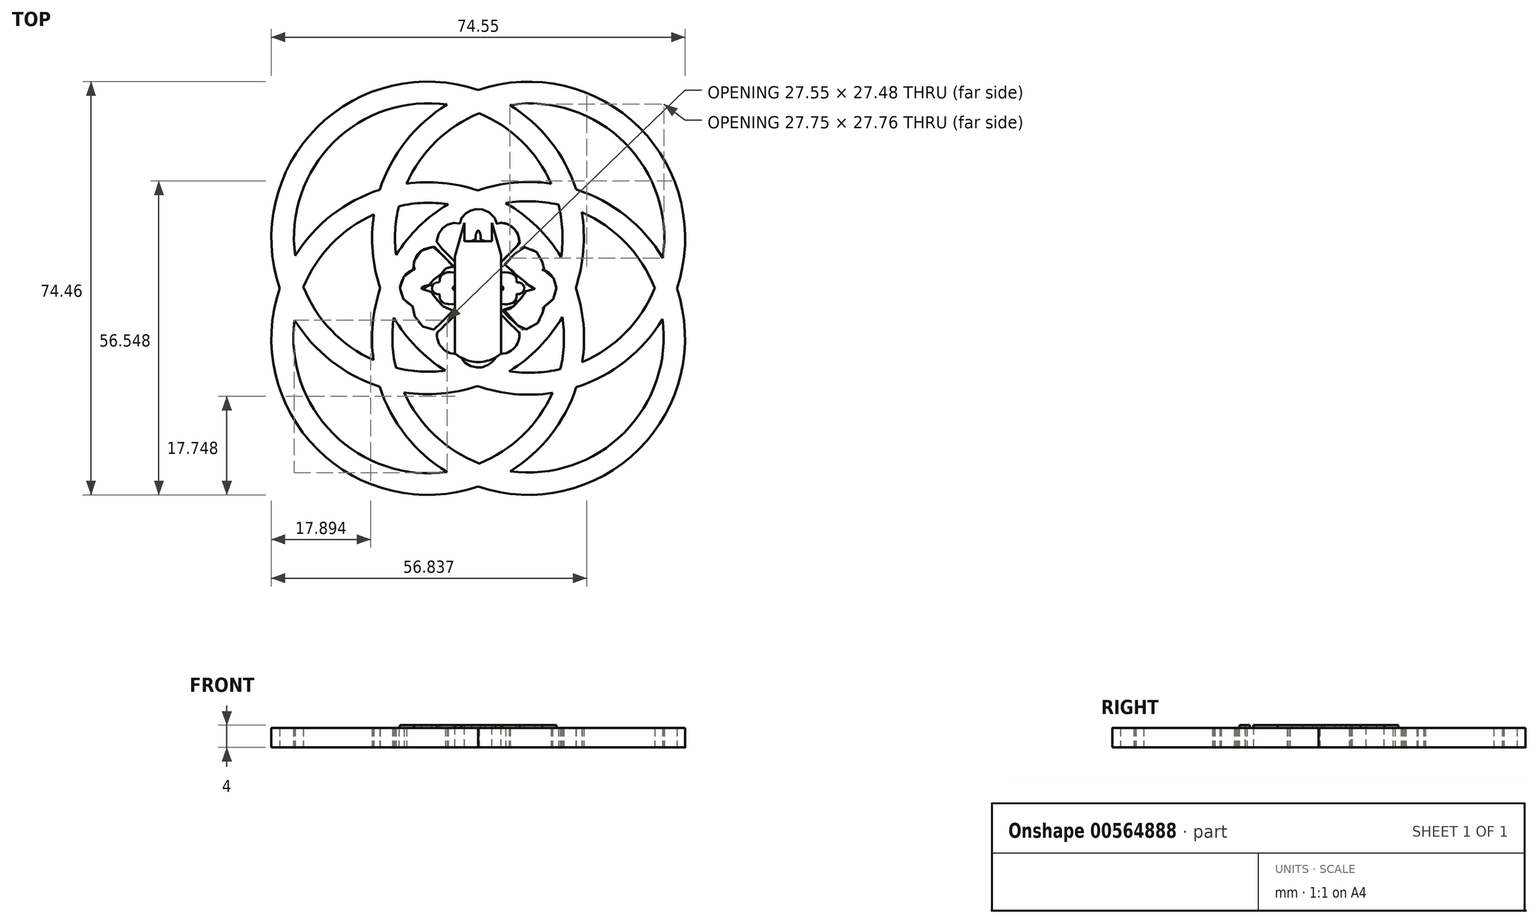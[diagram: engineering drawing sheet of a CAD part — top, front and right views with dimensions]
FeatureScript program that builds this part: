
annotation { "Feature Type Name" : "Feature", "Feature Type Description" : "" }
export const myFeature = defineFeature(function(context is Context, id is Id, definition is map)
    precondition{}
    {
        {
            var Q0;
            Q0=qCreatedBy(makeId("Top.planeOp"),FACE);
            var sketch = newSketch(context, id + "F0", { "sketchPlane" : qUnion([Q0])});
            skCircle(sketch, "E0", {"center": v(-9.1, 9.06) * mm, "radius": 28.15 * mm});
            skPoint(sketch, "E0.first.point", {"position": v(-26.2, 31.43) * mm});
            skPoint(sketch, "E0.second.point", {"position": v(8.54, -12.88) * mm});
            skPoint(sketch, "E0.third.point", {"position": v(14.56, 24.33) * mm});
            skCircle(sketch, "E1", {"center": v(-8.98, 9.13) * mm, "radius": 24.19 * mm});
            skPoint(sketch, "E1.first.point", {"position": v(-26.7, 25.61) * mm});
            skPoint(sketch, "E1.second.point", {"position": v(8.44, -7.65) * mm});
            skPoint(sketch, "E1.third.point", {"position": v(11, 22.75) * mm});
            skSolve(sketch);
        }
        {
            var Q0;
            Q0 = qSketchRegion(id + "F0", true);
            extrude(context, id + "F1", {"entities" : qUnion([Q0]), "depth" : 3.5 * mm, "offsetDistance" : 25.4 * mm});
        }
        {
            var Q0;
            Q0=qCreatedBy(makeId("Top.planeOp"),FACE);
            var sketch = newSketch(context, id + "F2", { "sketchPlane" : qUnion([Q0])});
            skCircle(sketch, "E2", {"center": v(9.1, 9.01) * mm, "radius": 28.2 * mm});
            skPoint(sketch, "E2.first.point", {"position": v(26.2, 31.43) * mm});
            skPoint(sketch, "E2.second.point", {"position": v(-8.04, -13.37) * mm});
            skPoint(sketch, "E2.third.point", {"position": v(26.99, -12.78) * mm});
            skCircle(sketch, "E3", {"center": v(9.29, 9.03) * mm, "radius": 24.25 * mm});
            skPoint(sketch, "E3.first.point", {"position": v(19.69, 30.93) * mm});
            skPoint(sketch, "E3.second.point", {"position": v(-1.33, -12.78) * mm});
            skPoint(sketch, "E3.third.point", {"position": v(-13.47, 17.42) * mm});
            skSolve(sketch);
        }
        {
            var Q0;
            Q0 = qSketchRegion(id + "F2", true);
            extrude(context, id + "F3", {"entities" : qUnion([Q0]), "operationType" : NewBodyOperationType.ADD, "depth" : 3.5 * mm, "offsetDistance" : 25.4 * mm});
        }
        {
            var Q0;
            Q0=qCreatedBy(makeId("Top.planeOp"),FACE);
            var sketch = newSketch(context, id + "F4", { "sketchPlane" : qUnion([Q0])});
            skCircle(sketch, "E4", {"center": v(9.08, -9.04) * mm, "radius": 28.19 * mm});
            skPoint(sketch, "E4.first.point", {"position": v(-3.51, 16.18) * mm});
            skPoint(sketch, "E4.second.point", {"position": v(21.62, -34.29) * mm});
            skPoint(sketch, "E4.third.point", {"position": v(37.25, -8.26) * mm});
            skCircle(sketch, "E5", {"center": v(9, -8.77) * mm, "radius": 24.44 * mm});
            skPoint(sketch, "E5.first.point", {"position": v(8.86, 15.67) * mm});
            skPoint(sketch, "E5.second.point", {"position": v(8.96, -33.2) * mm});
            skPoint(sketch, "E5.third.point", {"position": v(32.01, -16.98) * mm});
            skSolve(sketch);
        }
        {
            var Q0;
            Q0 = qSketchRegion(id + "F4", true);
            extrude(context, id + "F5", {"entities" : qUnion([Q0]), "operationType" : NewBodyOperationType.ADD, "depth" : 3.5 * mm, "offsetDistance" : 25.4 * mm});
        }
        {
            var Q0;
            Q0=qCreatedBy(makeId("Top.planeOp"),FACE);
            var sketch = newSketch(context, id + "F6", { "sketchPlane" : qUnion([Q0])});
            skCircle(sketch, "E6", {"center": v(-9.08, -9.07) * mm, "radius": 28.16 * mm});
            skPoint(sketch, "E6.first.point", {"position": v(-28.54, 11.29) * mm});
            skPoint(sketch, "E6.second.point", {"position": v(10.5, -29.33) * mm});
            skPoint(sketch, "E6.third.point", {"position": v(18.98, -6.56) * mm});
            skCircle(sketch, "E7", {"center": v(-8.9, -8.98) * mm, "radius": 24.36 * mm});
            skPoint(sketch, "E7.first.point", {"position": v(-28.73, 5.17) * mm});
            skPoint(sketch, "E7.second.point", {"position": v(10.8, -23.32) * mm});
            skPoint(sketch, "E7.third.point", {"position": v(-18.87, -31.2) * mm});
            skSolve(sketch);
        }
        {
            var Q0;
            Q0 = qSketchRegion(id + "F6", true);
            extrude(context, id + "F7", {"entities" : qUnion([Q0]), "operationType" : NewBodyOperationType.ADD, "depth" : 3.5 * mm, "offsetDistance" : 25.4 * mm});
        }
        {
            var Q0;
            Q0=qCreatedBy(makeId("Top.planeOp"),FACE);
            var sketch = newSketch(context, id + "F8", { "sketchPlane" : qUnion([Q0])});
            skCircle(sketch, "E8", {"center": v(0, 0) * mm, "radius": 14.23 * mm});
            skSolve(sketch);
        }
        {
            var Q0;
            Q0 = qSketchRegion(id + "F8", true);
            extrude(context, id + "F9", {"entities" : qUnion([Q0]), "operationType" : NewBodyOperationType.ADD, "depth" : 3.5 * mm, "offsetDistance" : 25.4 * mm});
        }
        {
            var Q0;
            Q0=makeQuery(id+"F9.boolean.opBoolean","MERGE",FACE,{"derivedFrom":[makeQuery(id+"F7.boolean.opBoolean","MERGE",FACE,{"derivedFrom":[makeQuery(id+"F5.boolean.opBoolean","MERGE",FACE,{"derivedFrom":[makeQuery(id+"F3.boolean.opBoolean","MERGE",FACE,{"derivedFrom":[makeQuery(id+"F1.opExtrude","CAP_FACE",FACE,{"disambiguationData":[OSD([sQuery(id+"F0.wireOp",EDGE,"E0"),sQuery(id+"F0.wireOp",EDGE,"E1")])],"isStart":false}),makeQuery(id+"F3.opExtrude","CAP_FACE",FACE,{"disambiguationData":[OSD([sQuery(id+"F2.wireOp",EDGE,"E2"),sQuery(id+"F2.wireOp",EDGE,"E3")])],"isStart":false})]}),makeQuery(id+"F5.opExtrude","CAP_FACE",FACE,{"disambiguationData":[OSD([sQuery(id+"F4.wireOp",EDGE,"E4"),sQuery(id+"F4.wireOp",EDGE,"E5")])],"isStart":false})]}),makeQuery(id+"F7.opExtrude","CAP_FACE",FACE,{"disambiguationData":[OSD([sQuery(id+"F6.wireOp",EDGE,"E6"),sQuery(id+"F6.wireOp",EDGE,"E7")])],"isStart":false})]}),makeQuery(id+"F9.opExtrude","CAP_FACE",FACE,{"disambiguationData":[OSD([sQuery(id+"F8.wireOp",EDGE,"E8")])],"isStart":false})]});
            var sketch = newSketch(context, id + "F10", { "sketchPlane" : qUnion([Q0])});
            skCircle(sketch, "E9", {"center": v(0, 0) * mm, "radius": 1.58 * mm});
            skSolve(sketch);
        }
        {
            var Q0;
            Q0 = qSketchRegion(id + "F10", true);
            extrude(context, id + "F11", {"entities" : qUnion([Q0]), "operationType" : NewBodyOperationType.ADD, "depth" : .5 * mm, "offsetDistance" : 25.4 * mm});
        }
        {
            var Q0;
            Q0=makeQuery(id+"F9.boolean.opBoolean","MERGE",FACE,{"derivedFrom":[makeQuery(id+"F7.boolean.opBoolean","MERGE",FACE,{"derivedFrom":[makeQuery(id+"F5.boolean.opBoolean","MERGE",FACE,{"derivedFrom":[makeQuery(id+"F3.boolean.opBoolean","MERGE",FACE,{"derivedFrom":[makeQuery(id+"F1.opExtrude","CAP_FACE",FACE,{"disambiguationData":[OSD([sQuery(id+"F0.wireOp",EDGE,"E0"),sQuery(id+"F0.wireOp",EDGE,"E1")])],"isStart":false}),makeQuery(id+"F3.opExtrude","CAP_FACE",FACE,{"disambiguationData":[OSD([sQuery(id+"F2.wireOp",EDGE,"E2"),sQuery(id+"F2.wireOp",EDGE,"E3")])],"isStart":false})]}),makeQuery(id+"F5.opExtrude","CAP_FACE",FACE,{"disambiguationData":[OSD([sQuery(id+"F4.wireOp",EDGE,"E4"),sQuery(id+"F4.wireOp",EDGE,"E5")])],"isStart":false})]}),makeQuery(id+"F7.opExtrude","CAP_FACE",FACE,{"disambiguationData":[OSD([sQuery(id+"F6.wireOp",EDGE,"E6"),sQuery(id+"F6.wireOp",EDGE,"E7")])],"isStart":false})]}),makeQuery(id+"F9.opExtrude","CAP_FACE",FACE,{"disambiguationData":[OSD([sQuery(id+"F8.wireOp",EDGE,"E8")])],"isStart":false})]});
            var sketch = newSketch(context, id + "F12", { "sketchPlane" : qUnion([Q0])});
            skFitSpline(sketch, "E10", {"points": [v(0.33, 4.4) * mm, v(0.5, 4.13) * mm, v(0.55, 3.94) * mm, v(0.65, 3.62) * mm, v(0.66, 3.35) * mm, v(0.63, 3.18) * mm, v(0.82, 3.05) * mm, v(1.1, 2.88) * mm, v(1.47, 2.83) * mm, v(1.85, 2.9) * mm, v(2.12, 3.05) * mm, v(2.4, 3.41) * mm, v(2.66, 3.8) * mm, v(2.8, 4.2) * mm, v(2.9, 4.86) * mm, v(2.77, 5.82) * mm, v(2.6, 6.3) * mm, v(2.26, 6.62) * mm, v(2.02, 6.81) * mm, v(1.72, 6.94) * mm, v(1.3, 6.92) * mm, v(1.12, 6.92) * mm, v(1.1, 7.37) * mm, v(0.99, 7.65) * mm, v(0.84, 7.9) * mm, v(0.66, 8.09) * mm, v(0.44, 8.24) * mm, v(0.19, 8.34) * mm, v(-0.13, 8.35) * mm, v(-0.48, 8.18) * mm, v(-0.75, 7.98) * mm, v(-0.9, 7.8) * mm, v(-1, 7.62) * mm, v(-1.08, 7.36) * mm, v(-1.1, 7.13) * mm, v(-1.1, 6.95) * mm, v(-1.34, 6.92) * mm, v(-1.58, 6.92) * mm, v(-1.87, 6.89) * mm, v(-2.01, 6.78) * mm, v(-2.26, 6.65) * mm, v(-2.53, 6.37) * mm, v(-2.65, 6.15) * mm, v(-2.7, 5.94) * mm, v(-2.82, 5.7) * mm, v(-2.87, 5.45) * mm, v(-2.88, 5.07) * mm, v(-2.9, 4.7) * mm, v(-2.83, 4.23) * mm, v(-2.66, 3.8) * mm, v(-2.47, 3.48) * mm, v(-2.28, 3.21) * mm, v(-1.94, 2.97) * mm, v(-1.52, 2.83) * mm, v(-1.18, 2.84) * mm, v(-0.9, 2.96) * mm, v(-0.67, 3.12) * mm, v(-0.63, 3.38) * mm, v(-0.61, 3.62) * mm, v(-0.54, 3.88) * mm, v(-0.46, 4.15) * mm, v(-0.33, 4.38) * mm, v(-0.2, 4.47) * mm, v(0, 4.5) * mm, v(0.16, 4.5) * mm, v(0.33, 4.4) * mm]});
            skSolve(sketch);
        }
        {
            var Q0;
            Q0 = qSketchRegion(id + "F12", true);
            extrude(context, id + "F13", {"entities" : qUnion([Q0]), "operationType" : NewBodyOperationType.ADD, "depth" : 0.5 * mm, "offsetDistance" : 25.4 * mm});
        }
        {
            var Q0;
            Q0=makeQuery(id+"F9.boolean.opBoolean","MERGE",FACE,{"derivedFrom":[makeQuery(id+"F7.boolean.opBoolean","MERGE",FACE,{"derivedFrom":[makeQuery(id+"F5.boolean.opBoolean","MERGE",FACE,{"derivedFrom":[makeQuery(id+"F3.boolean.opBoolean","MERGE",FACE,{"derivedFrom":[makeQuery(id+"F1.opExtrude","CAP_FACE",FACE,{"disambiguationData":[OSD([sQuery(id+"F0.wireOp",EDGE,"E0"),sQuery(id+"F0.wireOp",EDGE,"E1")])],"isStart":false}),makeQuery(id+"F3.opExtrude","CAP_FACE",FACE,{"disambiguationData":[OSD([sQuery(id+"F2.wireOp",EDGE,"E2"),sQuery(id+"F2.wireOp",EDGE,"E3")])],"isStart":false})]}),makeQuery(id+"F5.opExtrude","CAP_FACE",FACE,{"disambiguationData":[OSD([sQuery(id+"F4.wireOp",EDGE,"E4"),sQuery(id+"F4.wireOp",EDGE,"E5")])],"isStart":false})]}),makeQuery(id+"F7.opExtrude","CAP_FACE",FACE,{"disambiguationData":[OSD([sQuery(id+"F6.wireOp",EDGE,"E6"),sQuery(id+"F6.wireOp",EDGE,"E7")])],"isStart":false})]}),makeQuery(id+"F9.opExtrude","CAP_FACE",FACE,{"disambiguationData":[OSD([sQuery(id+"F8.wireOp",EDGE,"E8")])],"isStart":false})]});
            var sketch = newSketch(context, id + "F14", { "sketchPlane" : qUnion([Q0])});
            skFitSpline(sketch, "E11", {"points": [v(4.64, -2.9) * mm, v(5.07, -2.9) * mm, v(5.36, -2.89) * mm, v(5.63, -2.82) * mm, v(5.98, -2.73) * mm, v(6.24, -2.64) * mm, v(6.42, -2.5) * mm, v(6.66, -2.26) * mm, v(6.83, -2.03) * mm, v(6.86, -1.83) * mm, v(6.91, -1.57) * mm, v(6.9, -1.3) * mm, v(6.87, -1.1) * mm, v(7.05, -1.1) * mm, v(7.34, -1.1) * mm, v(7.7, -1) * mm, v(8, -0.76) * mm, v(8.23, -0.45) * mm, v(8.34, -0.15) * mm, v(8.32, 0.13) * mm, v(8.31, 0.32) * mm, v(8.16, 0.52) * mm, v(8.02, 0.7) * mm, v(7.86, 0.86) * mm, v(7.6, 0.99) * mm, v(7.35, 1.06) * mm, v(7.15, 1.09) * mm, v(6.95, 1.06) * mm, v(6.89, 1.06) * mm, v(6.92, 1.2) * mm, v(6.92, 1.7) * mm, v(6.8, 2.09) * mm, v(6.57, 2.39) * mm, v(6.16, 2.63) * mm, v(5.78, 2.78) * mm, v(5.3, 2.86) * mm, v(4.84, 2.9) * mm, v(4.35, 2.85) * mm, v(4, 2.76) * mm, v(3.5, 2.51) * mm, v(3.2, 2.25) * mm, v(2.93, 1.9) * mm, v(2.82, 1.61) * mm, v(2.83, 1.24) * mm, v(3, 0.87) * mm, v(3.26, 0.63) * mm, v(3.63, 0.62) * mm, v(3.85, 0.55) * mm, v(4.15, 0.47) * mm, v(4.32, 0.34) * mm, v(4.5, 0.2) * mm, v(4.52, 0) * mm, v(4.54, -0.13) * mm, v(4.42, -0.29) * mm, v(4.22, -0.42) * mm, v(3.9, -0.54) * mm, v(3.7, -0.62) * mm, v(3.43, -0.66) * mm, v(3.2, -0.65) * mm, v(3.05, -0.8) * mm, v(2.86, -1.1) * mm, v(2.8, -1.38) * mm, v(2.86, -1.73) * mm, v(3.02, -2.07) * mm, v(3.26, -2.36) * mm, v(3.59, -2.6) * mm, v(3.9, -2.73) * mm, v(4.26, -2.86) * mm, v(4.64, -2.9) * mm]});
            skSolve(sketch);
        }
        {
            var Q0;
            Q0=makeQuery(id+"F14.imprint","IMPRINT",FACE,{"disambiguationData":[TD([[makeQuery(id+"F14.imprint","IMPRINT",EDGE,{"derivedFrom":sQuery(id+"F14.wireOp",EDGE,"E11")}),1.0]])]});
            extrude(context, id + "F15", {"entities" : qUnion([Q0]), "operationType" : NewBodyOperationType.ADD, "depth" : 0.5 * mm, "offsetDistance" : 25.4 * mm});
        }
        {
            var Q0;
            Q0=makeQuery(id+"F9.boolean.opBoolean","MERGE",FACE,{"derivedFrom":[makeQuery(id+"F7.boolean.opBoolean","MERGE",FACE,{"derivedFrom":[makeQuery(id+"F5.boolean.opBoolean","MERGE",FACE,{"derivedFrom":[makeQuery(id+"F3.boolean.opBoolean","MERGE",FACE,{"derivedFrom":[makeQuery(id+"F1.opExtrude","CAP_FACE",FACE,{"disambiguationData":[OSD([sQuery(id+"F0.wireOp",EDGE,"E0"),sQuery(id+"F0.wireOp",EDGE,"E1")])],"isStart":false}),makeQuery(id+"F3.opExtrude","CAP_FACE",FACE,{"disambiguationData":[OSD([sQuery(id+"F2.wireOp",EDGE,"E2"),sQuery(id+"F2.wireOp",EDGE,"E3")])],"isStart":false})]}),makeQuery(id+"F5.opExtrude","CAP_FACE",FACE,{"disambiguationData":[OSD([sQuery(id+"F4.wireOp",EDGE,"E4"),sQuery(id+"F4.wireOp",EDGE,"E5")])],"isStart":false})]}),makeQuery(id+"F7.opExtrude","CAP_FACE",FACE,{"disambiguationData":[OSD([sQuery(id+"F6.wireOp",EDGE,"E6"),sQuery(id+"F6.wireOp",EDGE,"E7")])],"isStart":false})]}),makeQuery(id+"F9.opExtrude","CAP_FACE",FACE,{"disambiguationData":[OSD([sQuery(id+"F8.wireOp",EDGE,"E8")])],"isStart":false})]});
            var sketch = newSketch(context, id + "F16", { "sketchPlane" : qUnion([Q0])});
            skFitSpline(sketch, "E12", {"points": [v(0, -8.37) * mm, v(0.26, -8.35) * mm, v(0.5, -8.23) * mm, v(0.79, -7.96) * mm, v(0.96, -7.7) * mm, v(1.05, -7.52) * mm, v(1.1, -7.1) * mm, v(1.08, -6.93) * mm, v(1.4, -6.94) * mm, v(1.88, -6.9) * mm, v(2.25, -6.68) * mm, v(2.6, -6.26) * mm, v(2.8, -5.71) * mm, v(2.9, -5.12) * mm, v(2.87, -4.5) * mm, v(2.73, -3.9) * mm, v(2.46, -3.43) * mm, v(2.16, -3.1) * mm, v(1.82, -2.92) * mm, v(1.46, -2.84) * mm, v(1.2, -2.87) * mm, v(0.94, -2.96) * mm, v(0.78, -3.08) * mm, v(0.69, -3.23) * mm, v(0.64, -3.4) * mm, v(0.64, -3.66) * mm, v(0.54, -3.95) * mm, v(0.45, -4.22) * mm, v(0.3, -4.42) * mm, v(0.1, -4.51) * mm, v(0, -4.52) * mm, v(-0.2, -4.46) * mm, v(-0.4, -4.24) * mm, v(-0.54, -3.94) * mm, v(-0.6, -3.72) * mm, v(-0.63, -3.49) * mm, v(-0.63, -3.26) * mm, v(-0.84, -3) * mm, v(-1.1, -2.9) * mm, v(-1.48, -2.82) * mm, v(-1.84, -2.93) * mm, v(-2.16, -3.1) * mm, v(-2.42, -3.4) * mm, v(-2.66, -3.8) * mm, v(-2.86, -4.28) * mm, v(-2.92, -4.63) * mm, v(-2.9, -5.08) * mm, v(-2.82, -5.64) * mm, v(-2.69, -6.14) * mm, v(-2.38, -6.55) * mm, v(-1.97, -6.84) * mm, v(-1.66, -6.94) * mm, v(-1.29, -6.93) * mm, v(-1.1, -6.91) * mm, v(-1.1, -7.1) * mm, v(-1.04, -7.58) * mm, v(-0.87, -7.86) * mm, v(-0.66, -8.1) * mm, v(-0.34, -8.31) * mm, v(-0.09, -8.36) * mm, v(0, -8.37) * mm]});
            skSolve(sketch);
        }
        {
            var Q0;
            Q0 = qSketchRegion(id + "F16", true);
            extrude(context, id + "F17", {"entities" : qUnion([Q0]), "operationType" : NewBodyOperationType.ADD, "depth" : 0.5 * mm, "offsetDistance" : 25.4 * mm});
        }
        {
            var Q0;
            Q0=makeQuery(id+"F9.boolean.opBoolean","MERGE",FACE,{"derivedFrom":[makeQuery(id+"F7.boolean.opBoolean","MERGE",FACE,{"derivedFrom":[makeQuery(id+"F5.boolean.opBoolean","MERGE",FACE,{"derivedFrom":[makeQuery(id+"F3.boolean.opBoolean","MERGE",FACE,{"derivedFrom":[makeQuery(id+"F1.opExtrude","CAP_FACE",FACE,{"disambiguationData":[OSD([sQuery(id+"F0.wireOp",EDGE,"E0"),sQuery(id+"F0.wireOp",EDGE,"E1")])],"isStart":false}),makeQuery(id+"F3.opExtrude","CAP_FACE",FACE,{"disambiguationData":[OSD([sQuery(id+"F2.wireOp",EDGE,"E2"),sQuery(id+"F2.wireOp",EDGE,"E3")])],"isStart":false})]}),makeQuery(id+"F5.opExtrude","CAP_FACE",FACE,{"disambiguationData":[OSD([sQuery(id+"F4.wireOp",EDGE,"E4"),sQuery(id+"F4.wireOp",EDGE,"E5")])],"isStart":false})]}),makeQuery(id+"F7.opExtrude","CAP_FACE",FACE,{"disambiguationData":[OSD([sQuery(id+"F6.wireOp",EDGE,"E6"),sQuery(id+"F6.wireOp",EDGE,"E7")])],"isStart":false})]}),makeQuery(id+"F9.opExtrude","CAP_FACE",FACE,{"disambiguationData":[OSD([sQuery(id+"F8.wireOp",EDGE,"E8")])],"isStart":false})]});
            var sketch = newSketch(context, id + "F18", { "sketchPlane" : qUnion([Q0])});
            skFitSpline(sketch, "E13", {"points": [v(-8.33, 0) * mm, v(-8.3, 0.25) * mm, v(-8.2, 0.48) * mm, v(-8.05, 0.7) * mm, v(-7.82, 0.9) * mm, v(-7.59, 1) * mm, v(-7.34, 1.05) * mm, v(-6.91, 1.07) * mm, v(-6.94, 1.24) * mm, v(-6.95, 1.44) * mm, v(-6.9, 1.78) * mm, v(-6.81, 2.02) * mm, v(-6.62, 2.3) * mm, v(-6.44, 2.5) * mm, v(-6.12, 2.65) * mm, v(-5.73, 2.8) * mm, v(-5.26, 2.88) * mm, v(-4.61, 2.9) * mm, v(-3.98, 2.78) * mm, v(-3.68, 2.59) * mm, v(-3.29, 2.34) * mm, v(-3, 2.03) * mm, v(-2.85, 1.67) * mm, v(-2.81, 1.28) * mm, v(-2.91, 1) * mm, v(-3.08, 0.73) * mm, v(-3.32, 0.63) * mm, v(-3.55, 0.63) * mm, v(-3.9, 0.56) * mm, v(-4.25, 0.4) * mm, v(-4.44, 0.28) * mm, v(-4.52, 0.16) * mm, v(-4.54, 0) * mm, v(-4.52, -0.12) * mm, v(-4.38, -0.31) * mm, v(-3.9, -0.54) * mm, v(-3.64, -0.6) * mm, v(-3.27, -0.66) * mm, v(-3.12, -0.68) * mm, v(-2.95, -0.97) * mm, v(-2.8, -1.3) * mm, v(-2.8, -1.62) * mm, v(-3, -2.05) * mm, v(-3.2, -2.31) * mm, v(-3.53, -2.55) * mm, v(-3.95, -2.76) * mm, v(-4.39, -2.88) * mm, v(-4.95, -2.9) * mm, v(-5.5, -2.85) * mm, v(-6, -2.76) * mm, v(-6.41, -2.5) * mm, v(-6.72, -2.16) * mm, v(-6.91, -1.85) * mm, v(-6.93, -1.4) * mm, v(-6.89, -1.13) * mm, v(-7.11, -1.08) * mm, v(-7.4, -1.08) * mm, v(-7.7, -0.95) * mm, v(-8.04, -0.73) * mm, v(-8.24, -0.38) * mm, v(-8.32, -0.23) * mm, v(-8.33, 0) * mm]});
            skSolve(sketch);
        }
        {
            var Q0;
            Q0=makeQuery(id+"F18.imprint","IMPRINT",FACE,{"disambiguationData":[TD([[makeQuery(id+"F18.imprint","IMPRINT",EDGE,{"derivedFrom":sQuery(id+"F18.wireOp",EDGE,"E13")}),-1.0]])]});
            extrude(context, id + "F19", {"entities" : qUnion([Q0]), "operationType" : NewBodyOperationType.ADD, "depth" : 0.5 * mm, "offsetDistance" : 25.4 * mm});
        }
        {
            var Q0;
            Q0=makeQuery(id+"F9.boolean.opBoolean","MERGE",FACE,{"derivedFrom":[makeQuery(id+"F7.boolean.opBoolean","MERGE",FACE,{"derivedFrom":[makeQuery(id+"F5.boolean.opBoolean","MERGE",FACE,{"derivedFrom":[makeQuery(id+"F3.boolean.opBoolean","MERGE",FACE,{"derivedFrom":[makeQuery(id+"F1.opExtrude","CAP_FACE",FACE,{"disambiguationData":[OSD([sQuery(id+"F0.wireOp",EDGE,"E0"),sQuery(id+"F0.wireOp",EDGE,"E1")])],"isStart":false}),makeQuery(id+"F3.opExtrude","CAP_FACE",FACE,{"disambiguationData":[OSD([sQuery(id+"F2.wireOp",EDGE,"E2"),sQuery(id+"F2.wireOp",EDGE,"E3")])],"isStart":false})]}),makeQuery(id+"F5.opExtrude","CAP_FACE",FACE,{"disambiguationData":[OSD([sQuery(id+"F4.wireOp",EDGE,"E4"),sQuery(id+"F4.wireOp",EDGE,"E5")])],"isStart":false})]}),makeQuery(id+"F7.opExtrude","CAP_FACE",FACE,{"disambiguationData":[OSD([sQuery(id+"F6.wireOp",EDGE,"E6"),sQuery(id+"F6.wireOp",EDGE,"E7")])],"isStart":false})]}),makeQuery(id+"F9.opExtrude","CAP_FACE",FACE,{"disambiguationData":[OSD([sQuery(id+"F8.wireOp",EDGE,"E8")])],"isStart":false})]});
            var sketch = newSketch(context, id + "F20", { "sketchPlane" : qUnion([Q0])});
            skFitSpline(sketch, "E14", {"points": [v(0, 14.29) * mm, v(0.61, 14.22) * mm, v(1.48, 13.97) * mm, v(2.13, 13.54) * mm, v(2.88, 12.8) * mm, v(3.16, 12.24) * mm, v(3.37, 11.62) * mm, v(3.64, 11.7) * mm, v(4.08, 11.77) * mm, v(4.67, 11.74) * mm, v(5.26, 11.58) * mm, v(6.05, 11.12) * mm, v(6.67, 10.49) * mm, v(7.08, 9.88) * mm, v(7.3, 9.21) * mm, v(7.44, 8.41) * mm, v(7.46, 8.03) * mm, v(7.29, 7.91) * mm, v(6.9, 7.5) * mm, v(6.18, 6.8) * mm, v(3.97, 4.64) * mm, v(3.85, 4.76) * mm, v(3.78, 5.4) * mm, v(3.67, 5.8) * mm, v(3.37, 6.3) * mm, v(2.99, 6.69) * mm, v(2.67, 6.9) * mm, v(2.3, 7.05) * mm, v(2.23, 7.2) * mm, v(1.98, 7.71) * mm, v(1.5, 8.24) * mm, v(1.1, 8.54) * mm, v(0.56, 8.67) * mm, v(0.47, 9.07) * mm, v(0.43, 9.51) * mm, v(0.36, 9.91) * mm, v(0.2, 10.22) * mm, v(0, 10.4) * mm, v(-0.2, 10.24) * mm, v(-0.3, 9.94) * mm, v(-0.43, 9.59) * mm, v(-0.44, 9.3) * mm, v(-0.49, 8.86) * mm, v(-0.53, 8.69) * mm, v(-0.84, 8.64) * mm, v(-1.12, 8.5) * mm, v(-1.54, 8.26) * mm, v(-1.86, 7.87) * mm, v(-2.02, 7.6) * mm, v(-2.23, 7.05) * mm, v(-2.4, 7) * mm, v(-2.88, 6.78) * mm, v(-3.2, 6.51) * mm, v(-3.44, 6.16) * mm, v(-3.62, 5.83) * mm, v(-3.77, 5.48) * mm, v(-3.78, 5.05) * mm, v(-3.85, 4.56) * mm, v(-4.24, 4.89) * mm, v(-7.43, 8.1) * mm, v(-7.47, 8.26) * mm, v(-7.4, 8.86) * mm, v(-7.03, 9.91) * mm, v(-6.7, 10.52) * mm, v(-6.25, 10.96) * mm, v(-5.75, 11.31) * mm, v(-5.18, 11.57) * mm, v(-4.5, 11.74) * mm, v(-3.9, 11.74) * mm, v(-3.32, 11.64) * mm, v(-3.3, 11.85) * mm, v(-3.15, 12.42) * mm, v(-2.72, 12.98) * mm, v(-2.32, 13.43) * mm, v(-1.83, 13.72) * mm, v(-1.44, 13.98) * mm, v(-0.94, 14.13) * mm, v(-0.55, 14.23) * mm, v(0, 14.29) * mm]});
            skSolve(sketch);
        }
        {
            var Q0;
            Q0 = qSketchRegion(id + "F20", true);
            extrude(context, id + "F21", {"entities" : qUnion([Q0]), "operationType" : NewBodyOperationType.ADD, "depth" : 0.5 * mm, "offsetDistance" : 25.4 * mm});
        }
        {
            var Q0;
            Q0=makeQuery(id+"F9.boolean.opBoolean","MERGE",FACE,{"derivedFrom":[makeQuery(id+"F7.boolean.opBoolean","MERGE",FACE,{"derivedFrom":[makeQuery(id+"F5.boolean.opBoolean","MERGE",FACE,{"derivedFrom":[makeQuery(id+"F3.boolean.opBoolean","MERGE",FACE,{"derivedFrom":[makeQuery(id+"F1.opExtrude","CAP_FACE",FACE,{"disambiguationData":[OSD([sQuery(id+"F0.wireOp",EDGE,"E0"),sQuery(id+"F0.wireOp",EDGE,"E1")])],"isStart":false}),makeQuery(id+"F3.opExtrude","CAP_FACE",FACE,{"disambiguationData":[OSD([sQuery(id+"F2.wireOp",EDGE,"E2"),sQuery(id+"F2.wireOp",EDGE,"E3")])],"isStart":false})]}),makeQuery(id+"F5.opExtrude","CAP_FACE",FACE,{"disambiguationData":[OSD([sQuery(id+"F4.wireOp",EDGE,"E4"),sQuery(id+"F4.wireOp",EDGE,"E5")])],"isStart":false})]}),makeQuery(id+"F7.opExtrude","CAP_FACE",FACE,{"disambiguationData":[OSD([sQuery(id+"F6.wireOp",EDGE,"E6"),sQuery(id+"F6.wireOp",EDGE,"E7")])],"isStart":false})]}),makeQuery(id+"F9.opExtrude","CAP_FACE",FACE,{"disambiguationData":[OSD([sQuery(id+"F8.wireOp",EDGE,"E8")])],"isStart":false})]});
            var sketch = newSketch(context, id + "F22", { "sketchPlane" : qUnion([Q0])});
            skFitSpline(sketch, "E15", {"points": [v(14.08, 0) * mm, v(14.04, -0.53) * mm, v(13.84, -1.4) * mm, v(13.26, -2.33) * mm, v(12.6, -2.92) * mm, v(11.9, -3.3) * mm, v(11.51, -3.38) * mm, v(11.53, -3.72) * mm, v(11.57, -4.34) * mm, v(11.45, -5.2) * mm, v(11.13, -5.8) * mm, v(10.58, -6.47) * mm, v(9.76, -7.05) * mm, v(8.72, -7.38) * mm, v(8, -7.42) * mm, v(7.85, -7.44) * mm, v(7.3, -6.87) * mm, v(4.48, -4.02) * mm, v(4.76, -3.86) * mm, v(5.38, -3.8) * mm, v(5.96, -3.56) * mm, v(6.51, -3.04) * mm, v(6.87, -2.39) * mm, v(7.21, -2.19) * mm, v(7.8, -1.83) * mm, v(8.23, -1.27) * mm, v(8.52, -0.6) * mm, v(9.02, -0.51) * mm, v(9.68, -0.38) * mm, v(10.16, -0.18) * mm, v(10.18, 0) * mm, v(10.08, 0.2) * mm, v(9.78, 0.34) * mm, v(9.48, 0.38) * mm, v(9.1, 0.46) * mm, v(8.5, 0.56) * mm, v(8.4, 0.82) * mm, v(8.17, 1.36) * mm, v(7.77, 1.81) * mm, v(7.23, 2.15) * mm, v(6.87, 2.35) * mm, v(6.57, 2.85) * mm, v(6.16, 3.3) * mm, v(5.5, 3.69) * mm, v(5.02, 3.83) * mm, v(4.42, 3.83) * mm, v(4.84, 4.32) * mm, v(5.76, 5.28) * mm, v(6.76, 6.32) * mm, v(7.84, 7.46) * mm, v(8.21, 7.46) * mm, v(9.04, 7.3) * mm, v(10.16, 6.87) * mm, v(10.92, 6.04) * mm, v(11.37, 5.32) * mm, v(11.57, 4.7) * mm, v(11.6, 3.8) * mm, v(11.51, 3.37) * mm, v(12, 3.2) * mm, v(12.77, 2.77) * mm, v(13.43, 2.02) * mm, v(13.85, 1.25) * mm, v(14.02, 0.68) * mm, v(14.08, 0) * mm]});
            skSolve(sketch);
        }
        {
            var Q0;
            Q0=makeQuery(id+"F22.imprint","IMPRINT",FACE,{"disambiguationData":[TD([[makeQuery(id+"F22.imprint","IMPRINT",EDGE,{"derivedFrom":sQuery(id+"F22.wireOp",EDGE,"E15")}),-1.0]])]});
            extrude(context, id + "F23", {"entities" : qUnion([Q0]), "operationType" : NewBodyOperationType.ADD, "depth" : 0.5 * mm, "offsetDistance" : 25.4 * mm});
        }
        {
            var Q0;
            Q0=makeQuery(id+"F9.boolean.opBoolean","MERGE",FACE,{"derivedFrom":[makeQuery(id+"F7.boolean.opBoolean","MERGE",FACE,{"derivedFrom":[makeQuery(id+"F5.boolean.opBoolean","MERGE",FACE,{"derivedFrom":[makeQuery(id+"F3.boolean.opBoolean","MERGE",FACE,{"derivedFrom":[makeQuery(id+"F1.opExtrude","CAP_FACE",FACE,{"disambiguationData":[OSD([sQuery(id+"F0.wireOp",EDGE,"E0"),sQuery(id+"F0.wireOp",EDGE,"E1")])],"isStart":false}),makeQuery(id+"F3.opExtrude","CAP_FACE",FACE,{"disambiguationData":[OSD([sQuery(id+"F2.wireOp",EDGE,"E2"),sQuery(id+"F2.wireOp",EDGE,"E3")])],"isStart":false})]}),makeQuery(id+"F5.opExtrude","CAP_FACE",FACE,{"disambiguationData":[OSD([sQuery(id+"F4.wireOp",EDGE,"E4"),sQuery(id+"F4.wireOp",EDGE,"E5")])],"isStart":false})]}),makeQuery(id+"F7.opExtrude","CAP_FACE",FACE,{"disambiguationData":[OSD([sQuery(id+"F6.wireOp",EDGE,"E6"),sQuery(id+"F6.wireOp",EDGE,"E7")])],"isStart":false})]}),makeQuery(id+"F9.opExtrude","CAP_FACE",FACE,{"disambiguationData":[OSD([sQuery(id+"F8.wireOp",EDGE,"E8")])],"isStart":false})]});
            var sketch = newSketch(context, id + "F24", { "sketchPlane" : qUnion([Q0])});
            skFitSpline(sketch, "E16", {"points": [v(0, -10.38) * mm, v(0.2, -10.27) * mm, v(0.38, -9.84) * mm, v(0.47, -9.18) * mm, v(0.53, -8.7) * mm, v(0.78, -8.69) * mm, v(1.07, -8.53) * mm, v(1.62, -8.18) * mm, v(1.96, -7.78) * mm, v(2.15, -7.44) * mm, v(2.3, -7.07) * mm, v(2.56, -6.98) * mm, v(2.98, -6.73) * mm, v(3.33, -6.4) * mm, v(3.58, -6.02) * mm, v(3.76, -5.58) * mm, v(3.84, -4.89) * mm, v(3.85, -4.62) * mm, v(4.55, -5.18) * mm, v(5.45, -6.12) * mm, v(6.55, -7.13) * mm, v(7.45, -8.13) * mm, v(7.47, -8.4) * mm, v(7.36, -9.16) * mm, v(7.13, -9.86) * mm, v(6.76, -10.44) * mm, v(6.18, -11.07) * mm, v(5.64, -11.4) * mm, v(4.93, -11.72) * mm, v(4.2, -11.76) * mm, v(3.58, -11.73) * mm, v(3.4, -11.69) * mm, v(3.27, -12.09) * mm, v(3.02, -12.67) * mm, v(2.45, -13.35) * mm, v(1.82, -13.77) * mm, v(1.33, -14.01) * mm, v(0.85, -14.2) * mm, v(0.6, -14.27) * mm, v(0, -14.27) * mm, v(-0.35, -14.26) * mm, v(-0.9, -14.13) * mm, v(-1.32, -14.03) * mm, v(-1.84, -13.75) * mm, v(-2.41, -13.37) * mm, v(-2.72, -13.03) * mm, v(-2.98, -12.64) * mm, v(-3.2, -12.18) * mm, v(-3.35, -11.7) * mm, v(-3.6, -11.75) * mm, v(-4.16, -11.8) * mm, v(-4.9, -11.72) * mm, v(-5.5, -11.49) * mm, v(-5.9, -11.29) * mm, v(-6.4, -10.84) * mm, v(-6.83, -10.32) * mm, v(-7.06, -9.96) * mm, v(-7.3, -9.3) * mm, v(-7.4, -8.7) * mm, v(-7.43, -8.08) * mm, v(-7.06, -7.7) * mm, v(-6.21, -6.88) * mm, v(-5.44, -6.13) * mm, v(-4.03, -4.73) * mm, v(-3.9, -4.65) * mm, v(-3.8, -4.76) * mm, v(-3.82, -5.1) * mm, v(-3.82, -5.35) * mm, v(-3.7, -5.8) * mm, v(-3.31, -6.42) * mm, v(-2.85, -6.82) * mm, v(-2.28, -7.08) * mm, v(-2.15, -7.34) * mm, v(-1.87, -7.8) * mm, v(-1.5, -8.23) * mm, v(-1.03, -8.57) * mm, v(-0.5, -8.69) * mm, v(-0.5, -8.84) * mm, v(-0.48, -9.3) * mm, v(-0.4, -9.84) * mm, v(-0.22, -10.26) * mm, v(0, -10.38) * mm]});
            skSolve(sketch);
        }
        {
            var Q0;
            Q0=makeQuery(id+"F24.imprint","IMPRINT",FACE,{"disambiguationData":[TD([[makeQuery(id+"F24.imprint","IMPRINT",EDGE,{"derivedFrom":sQuery(id+"F24.wireOp",EDGE,"E16")}),-1.0]])]});
            extrude(context, id + "F25", {"entities" : qUnion([Q0]), "operationType" : NewBodyOperationType.ADD, "depth" : 0.5 * mm, "offsetDistance" : 25.4 * mm});
        }
        {
            var Q0;
            Q0=makeQuery(id+"F9.boolean.opBoolean","MERGE",FACE,{"derivedFrom":[makeQuery(id+"F7.boolean.opBoolean","MERGE",FACE,{"derivedFrom":[makeQuery(id+"F5.boolean.opBoolean","MERGE",FACE,{"derivedFrom":[makeQuery(id+"F3.boolean.opBoolean","MERGE",FACE,{"derivedFrom":[makeQuery(id+"F1.opExtrude","CAP_FACE",FACE,{"disambiguationData":[OSD([sQuery(id+"F0.wireOp",EDGE,"E0"),sQuery(id+"F0.wireOp",EDGE,"E1")])],"isStart":false}),makeQuery(id+"F3.opExtrude","CAP_FACE",FACE,{"disambiguationData":[OSD([sQuery(id+"F2.wireOp",EDGE,"E2"),sQuery(id+"F2.wireOp",EDGE,"E3")])],"isStart":false})]}),makeQuery(id+"F5.opExtrude","CAP_FACE",FACE,{"disambiguationData":[OSD([sQuery(id+"F4.wireOp",EDGE,"E4"),sQuery(id+"F4.wireOp",EDGE,"E5")])],"isStart":false})]}),makeQuery(id+"F7.opExtrude","CAP_FACE",FACE,{"disambiguationData":[OSD([sQuery(id+"F6.wireOp",EDGE,"E6"),sQuery(id+"F6.wireOp",EDGE,"E7")])],"isStart":false})]}),makeQuery(id+"F9.opExtrude","CAP_FACE",FACE,{"disambiguationData":[OSD([sQuery(id+"F8.wireOp",EDGE,"E8")])],"isStart":false})]});
            var sketch = newSketch(context, id + "F26", { "sketchPlane" : qUnion([Q0])});
            skFitSpline(sketch, "E17", {"points": [v(-14.1, 0) * mm, v(-13.98, 0.57) * mm, v(-13.72, 1.39) * mm, v(-13.37, 2.06) * mm, v(-12.92, 2.63) * mm, v(-12.47, 2.94) * mm, v(-11.84, 3.24) * mm, v(-11.45, 3.35) * mm, v(-11.55, 3.7) * mm, v(-11.58, 4.39) * mm, v(-11.4, 5.14) * mm, v(-10.92, 6.04) * mm, v(-10.53, 6.47) * mm, v(-9.94, 6.96) * mm, v(-9.29, 7.18) * mm, v(-8.53, 7.39) * mm, v(-7.86, 7.43) * mm, v(-7.55, 7.14) * mm, v(-6.78, 6.35) * mm, v(-5.27, 4.8) * mm, v(-4.65, 4.16) * mm, v(-4.5, 3.98) * mm, v(-4.5, 3.86) * mm, v(-4.68, 3.82) * mm, v(-5, 3.84) * mm, v(-5.3, 3.8) * mm, v(-5.65, 3.63) * mm, v(-6.02, 3.43) * mm, v(-6.35, 3.22) * mm, v(-6.6, 2.9) * mm, v(-6.74, 2.6) * mm, v(-6.84, 2.3) * mm, v(-7.1, 2.16) * mm, v(-7.51, 1.98) * mm, v(-7.78, 1.75) * mm, v(-8, 1.55) * mm, v(-8.17, 1.33) * mm, v(-8.33, 0.96) * mm, v(-8.45, 0.55) * mm, v(-8.88, 0.5) * mm, v(-9.5, 0.43) * mm, v(-9.86, 0.32) * mm, v(-10.2, 0) * mm, v(-9.96, -0.23) * mm, v(-9.57, -0.37) * mm, v(-9.1, -0.47) * mm, v(-8.5, -0.53) * mm, v(-8.41, -0.74) * mm, v(-8.3, -1.08) * mm, v(-8.02, -1.51) * mm, v(-7.72, -1.84) * mm, v(-7.15, -2.19) * mm, v(-6.86, -2.29) * mm, v(-6.72, -2.6) * mm, v(-6.47, -3.08) * mm, v(-5.82, -3.6) * mm, v(-5.17, -3.82) * mm, v(-4.47, -3.92) * mm, v(-4.65, -4.2) * mm, v(-5.29, -4.86) * mm, v(-6.53, -6.1) * mm, v(-7.33, -6.92) * mm, v(-7.7, -7.31) * mm, v(-7.86, -7.43) * mm, v(-8.17, -7.45) * mm, v(-8.68, -7.43) * mm, v(-9.5, -7.19) * mm, v(-10.1, -6.82) * mm, v(-10.8, -6.23) * mm, v(-11.29, -5.5) * mm, v(-11.53, -4.6) * mm, v(-11.58, -3.98) * mm, v(-11.45, -3.43) * mm, v(-11.92, -3.29) * mm, v(-12.47, -3.02) * mm, v(-13.2, -2.3) * mm, v(-13.56, -1.8) * mm, v(-13.92, -1.1) * mm, v(-14.07, -0.45) * mm, v(-14.1, 0) * mm]});
            skSolve(sketch);
        }
        {
            var Q0;
            Q0=makeQuery(id+"F26.imprint","IMPRINT",FACE,{"disambiguationData":[TD([[makeQuery(id+"F26.imprint","IMPRINT",EDGE,{"derivedFrom":sQuery(id+"F26.wireOp",EDGE,"E17")}),-1.0]])]});
            extrude(context, id + "F27", {"entities" : qUnion([Q0]), "operationType" : NewBodyOperationType.ADD, "depth" : 0.5 * mm, "offsetDistance" : 25.4 * mm});
        }
        {
            var Q0;
            Q0=makeQuery(id+"F13.opExtrude","CAP_FACE",FACE,{"disambiguationData":[OSD([sQuery(id+"F12.wireOp",EDGE,"E10")])],"isStart":false});
            var sketch = newSketch(context, id + "F28", { "sketchPlane" : qUnion([Q0])});
            skLineSegment(sketch, "E18.bottom", {"start": v(-4.16, 11.75) * mm, "end": v(4.16, 11.75) * mm});
            skLineSegment(sketch, "E18.top", {"start": v(-4.16, -11.75) * mm, "end": v(4.16, -11.75) * mm});
            skLineSegment(sketch, "E18.left", {"start": v(-4.16, 11.75) * mm, "end": v(-4.16, -11.75) * mm});
            skLineSegment(sketch, "E18.right", {"start": v(4.16, 11.75) * mm, "end": v(4.16, -11.75) * mm});
            skPoint(sketch, "E18.middle", {"position": v(0, 0) * mm});
            skArc(sketch, "E19", {"start": v(-4.16, -11.75) * mm, "mid": v(0, -13.3) * mm, "end": v(4.16, -11.75) * mm});
            skLineSegment(sketch, "E20.bottom", {"start": v(-2.5, 11.75) * mm, "end": v(2.5, 11.75) * mm});
            skLineSegment(sketch, "E20.top", {"start": v(-2.5, 8.48) * mm, "end": v(2.5, 8.48) * mm});
            skLineSegment(sketch, "E20.left", {"start": v(-2.5, 11.75) * mm, "end": v(-2.5, 8.48) * mm});
            skLineSegment(sketch, "E20.right", {"start": v(2.5, 11.75) * mm, "end": v(2.5, 8.48) * mm});
            skLineSegment(sketch, "E21", {"start": v(-2.5, 11.75) * mm, "end": v(-4.16, 5.75) * mm});
            skLineSegment(sketch, "E22", {"start": v(-4.16, 5.75) * mm, "end": v(-2.5, 11.75) * mm});
            skLineSegment(sketch, "E23", {"start": v(2.5, 11.75) * mm, "end": v(4.16, 6) * mm});
            skLineSegment(sketch, "E24", {"start": v(4.16, 6) * mm, "end": v(2.5, 11.75) * mm});
            skSolve(sketch);
        }
        {
            var Q0;
            Q0=makeQuery(id+"F28.imprint","IMPRINT",FACE,{"disambiguationData":[TD([[makeQuery(id+"F28.imprint","IMPRINT",EDGE,{"derivedFrom":sQuery(id+"F28.wireOp",EDGE,"E20.bottom")}),-1.0]])]});
            var Q1;
            {var subQ2=sQuery(id+"F28.wireOp",EDGE,"E18.top");Q1=makeQuery(id+"F28.imprint","IMPRINT",FACE,{"disambiguationData":[TD([[makeQuery(id+"F28.imprint","IMPRINT",EDGE,{"derivedFrom":subQ2}),1.0]])]});}
            var Q2;
            Q2=makeQuery(id+"F28.imprint","IMPRINT",FACE,{"disambiguationData":[TD([[makeQuery(id+"F28.imprint","IMPRINT",EDGE,{"derivedFrom":makeQuery(id+"F13.opExtrude","CAP_EDGE",EDGE,{"disambiguationData":[OSD([sQuery(id+"F12.wireOp",EDGE,"E10")])],"isStart":false})}),1.0]])]});
            var Q3;
            Q3=makeQuery(id+"F28.imprint","IMPRINT",FACE,{"disambiguationData":[TD([[makeQuery(id+"F28.imprint","IMPRINT",EDGE,{"derivedFrom":sQuery(id+"F28.wireOp",EDGE,"E18.top")}),-1.0]])]});
            extrude(context, id + "F29", {"entities" : qUnion([Q0, Q1, Q2, Q3]), "operationType" : NewBodyOperationType.REMOVE, "endBound" : BoundingType.THROUGH_ALL, "oppositeDirection" : true, "depth" : 25.4 * mm, "offsetDistance" : 25.4 * mm});
        }
    });
